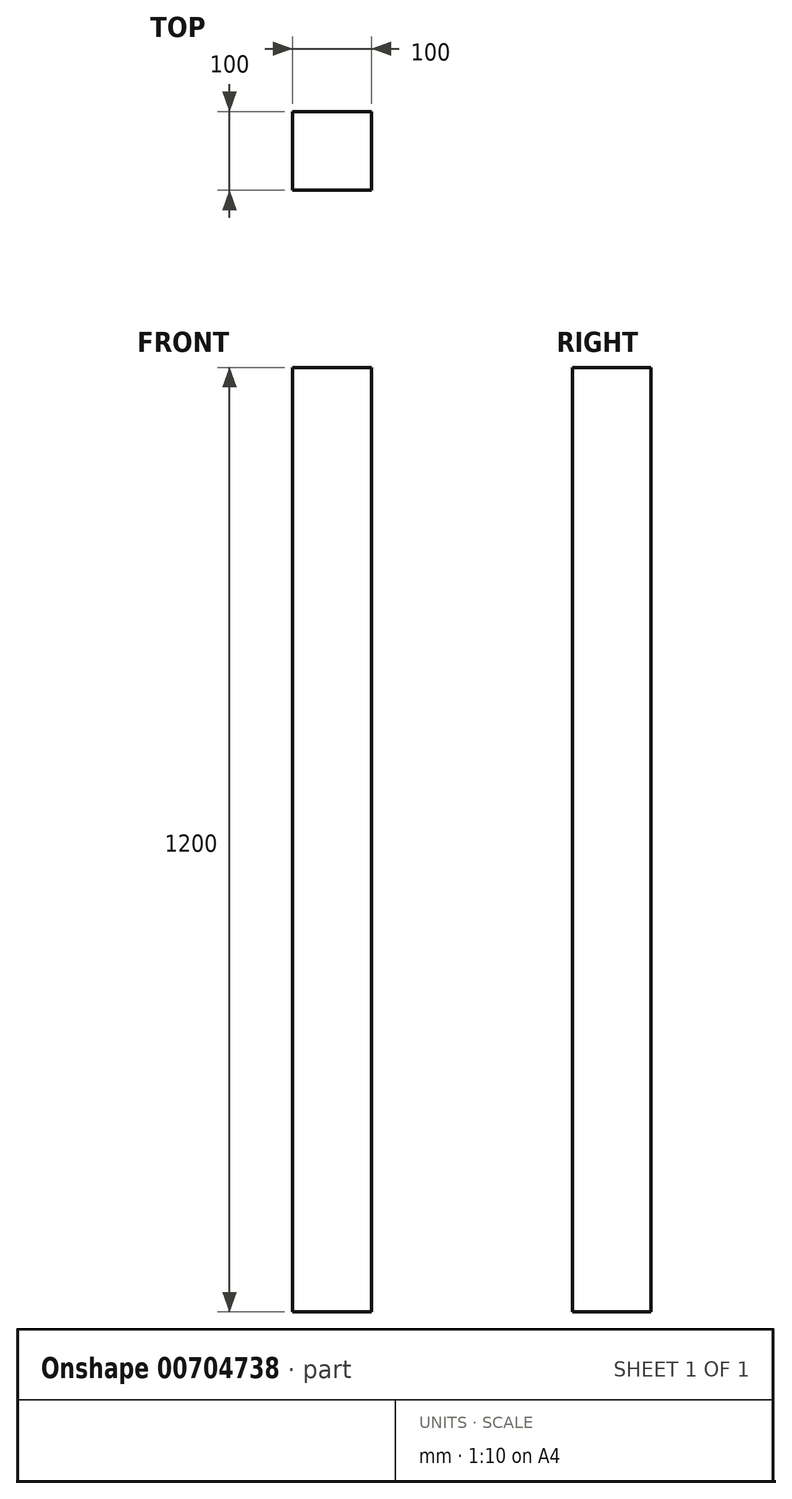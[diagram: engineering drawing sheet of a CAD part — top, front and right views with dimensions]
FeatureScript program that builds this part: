
annotation { "Feature Type Name" : "Feature", "Feature Type Description" : "" }
export const myFeature = defineFeature(function(context is Context, id is Id, definition is map)
    precondition{}
    {
        {
            var Q0;
            Q0=qCreatedBy(makeId("Top.planeOp"),FACE);
            var sketch = newSketch(context, id + "F0", { "sketchPlane" : qUnion([Q0])});
            skLineSegment(sketch, "E0.bottom", {"start": v(0, 0) * mm, "end": v(100, 0) * mm});
            skLineSegment(sketch, "E0.top", {"start": v(0, 100) * mm, "end": v(100, 100) * mm});
            skLineSegment(sketch, "E0.left", {"start": v(0, 0) * mm, "end": v(0, 100) * mm});
            skLineSegment(sketch, "E0.right", {"start": v(100, 0) * mm, "end": v(100, 100) * mm});
            skSolve(sketch);
        }
        {
            var Q0;
            Q0 = qSketchRegion(id + "F0", true);
            extrude(context, id + "F1", {"entities" : qUnion([Q0]), "depth" : 1200 * mm, "offsetDistance" : 25 * mm});
        }
    });
